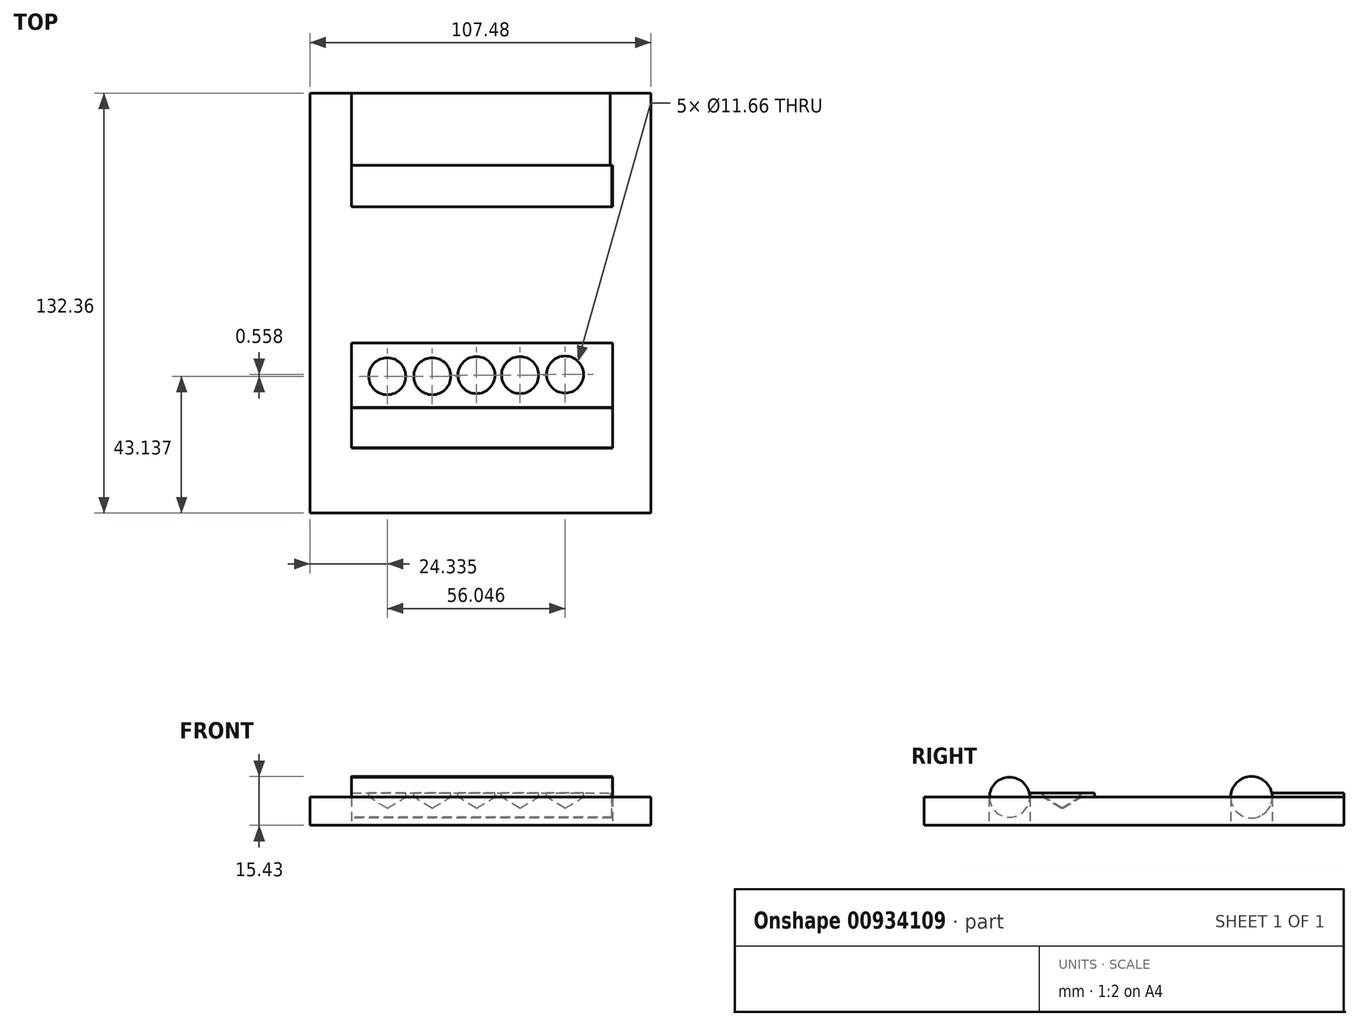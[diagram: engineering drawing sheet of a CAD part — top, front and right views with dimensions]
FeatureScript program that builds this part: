
annotation { "Feature Type Name" : "Feature", "Feature Type Description" : "" }
export const myFeature = defineFeature(function(context is Context, id is Id, definition is map)
    precondition{}
    {
        {
            var Q0;
            Q0=qCreatedBy(makeId("Top.planeOp"),FACE);
            var sketch = newSketch(context, id + "F0", { "sketchPlane" : qUnion([Q0])});
            skLineSegment(sketch, "E0.bottom", {"start": v(-52.45, 65.35) * mm, "end": v(55.03, 65.35) * mm});
            skLineSegment(sketch, "E0.top", {"start": v(-52.45, -67.01) * mm, "end": v(55.03, -67.01) * mm});
            skLineSegment(sketch, "E0.left", {"start": v(-52.45, 65.35) * mm, "end": v(-52.45, -67.01) * mm});
            skLineSegment(sketch, "E0.right", {"start": v(55.03, 65.35) * mm, "end": v(55.03, -67.01) * mm});
            skLineSegment(sketch, "E1.bottom", {"start": v(-39.36, 42.68) * mm, "end": v(42.86, 42.68) * mm});
            skLineSegment(sketch, "E1.top", {"start": v(-39.36, 29.59) * mm, "end": v(42.86, 29.59) * mm});
            skLineSegment(sketch, "E1.left", {"start": v(-39.36, 42.68) * mm, "end": v(-39.36, 29.59) * mm});
            skLineSegment(sketch, "E1.right", {"start": v(42.86, 42.68) * mm, "end": v(42.86, 29.59) * mm});
            skLineSegment(sketch, "E2.bottom", {"start": v(-39.36, -33.64) * mm, "end": v(42.86, -33.64) * mm});
            skLineSegment(sketch, "E2.top", {"start": v(-39.36, -46.55) * mm, "end": v(42.86, -46.55) * mm});
            skLineSegment(sketch, "E2.left", {"start": v(-39.36, -33.64) * mm, "end": v(-39.36, -46.55) * mm});
            skLineSegment(sketch, "E2.right", {"start": v(42.86, -33.64) * mm, "end": v(42.86, -46.55) * mm});
            skSolve(sketch);
        }
        {
            var Q0;
            Q0 = qSketchRegion(id + "F0", true);
            extrude(context, id + "F1", {"entities" : qUnion([Q0]), "depth" : 8.9 * mm, "offsetDistance" : 25.4 * mm});
        }
        {
            var Q0;
            Q0=makeQuery(id+"F1.opExtrude","SWEPT_FACE",FACE,{"disambiguationData":[OSD([sQuery(id+"F0.wireOp",EDGE,"E1.left")])]});
            var sketch = newSketch(context, id + "F2", { "sketchPlane" : qUnion([Q0])});
            skPoint(sketch, "E3", {"position": v(36.13, 8.9) * mm});
            skPoint(sketch, "E4", {"position": v(15.66, 189.85) * mm});
            skCircle(sketch, "E5", {"center": v(36.13, 8.9) * mm, "radius": 6.54 * mm});
            skSolve(sketch);
        }
        {
            var Q0;
            Q0 = qSketchRegion(id + "F2", true);
            extrude(context, id + "F3", {"entities" : qUnion([Q0]), "operationType" : NewBodyOperationType.ADD, "depth" : 82.04 * mm, "offsetDistance" : 25.4 * mm});
        }
        {
            var Q0;
            Q0=makeQuery(id+"F1.opExtrude","SWEPT_FACE",FACE,{"disambiguationData":[OSD([sQuery(id+"F0.wireOp",EDGE,"E2.left")])]});
            var sketch = newSketch(context, id + "F4", { "sketchPlane" : qUnion([Q0])});
            skPoint(sketch, "E6", {"position": v(-40.1, 8.9) * mm});
            skCircle(sketch, "E7", {"center": v(-40.1, 8.9) * mm, "radius": 6.32 * mm});
            skSolve(sketch);
        }
        {
            var Q0;
            Q0 = qSketchRegion(id + "F4", true);
            extrude(context, id + "F5", {"entities" : qUnion([Q0]), "operationType" : NewBodyOperationType.ADD, "depth" : 82.3 * mm, "offsetDistance" : 25.4 * mm});
        }
        {
            var Q0;
            Q0=makeQuery(id+"F1.opExtrude","CAP_FACE",FACE,{"disambiguationData":[OSD([sQuery(id+"F0.wireOp",EDGE,"E0.bottom"),sQuery(id+"F0.wireOp",EDGE,"E0.top"),sQuery(id+"F0.wireOp",EDGE,"E0.left"),sQuery(id+"F0.wireOp",EDGE,"E0.right"),sQuery(id+"F0.wireOp",EDGE,"E1.bottom"),sQuery(id+"F0.wireOp",EDGE,"E1.top"),sQuery(id+"F0.wireOp",EDGE,"E1.left"),sQuery(id+"F0.wireOp",EDGE,"E1.right"),sQuery(id+"F0.wireOp",EDGE,"E2.bottom"),sQuery(id+"F0.wireOp",EDGE,"E2.top"),sQuery(id+"F0.wireOp",EDGE,"E2.left"),sQuery(id+"F0.wireOp",EDGE,"E2.right")])],"isStart":false});
            var sketch = newSketch(context, id + "F6", { "sketchPlane" : qUnion([Q0])});
            skLineSegment(sketch, "E8.bottom", {"start": v(-39.36, 42.68) * mm, "end": v(42.17, 42.68) * mm});
            skLineSegment(sketch, "E8.top", {"start": v(-39.36, 65.35) * mm, "end": v(42.17, 65.35) * mm});
            skLineSegment(sketch, "E8.left", {"start": v(-39.36, 42.68) * mm, "end": v(-39.36, 65.35) * mm});
            skLineSegment(sketch, "E8.right", {"start": v(42.17, 42.68) * mm, "end": v(42.17, 65.35) * mm});
            skLineSegment(sketch, "E9.bottom", {"start": v(42.86, -33.64) * mm, "end": v(-39.36, -33.64) * mm});
            skLineSegment(sketch, "E9.top", {"start": v(42.86, -13.32) * mm, "end": v(-39.36, -13.32) * mm});
            skLineSegment(sketch, "E9.left", {"start": v(42.86, -33.64) * mm, "end": v(42.86, -13.32) * mm});
            skLineSegment(sketch, "E9.right", {"start": v(-39.36, -33.64) * mm, "end": v(-39.36, -13.32) * mm});
            skSolve(sketch);
        }
        {
            var Q0;
            Q0 = qSketchRegion(id + "F6", true);
            extrude(context, id + "F7", {"entities" : qUnion([Q0]), "operationType" : NewBodyOperationType.ADD, "depth" : 1.27 * mm, "offsetDistance" : 25.4 * mm});
        }
        {
            var Q0;
            Q0=makeQuery(id+"F7.opExtrude","CAP_FACE",FACE,{"disambiguationData":[OSD([sQuery(id+"F6.wireOp",EDGE,"E9.bottom"),sQuery(id+"F6.wireOp",EDGE,"E9.top"),sQuery(id+"F6.wireOp",EDGE,"E9.left"),sQuery(id+"F6.wireOp",EDGE,"E9.right")])],"isStart":false});
            var sketch = newSketch(context, id + "F8", { "sketchPlane" : qUnion([Q0])});
            skLineSegment(sketch, "E10.bottom", {"start": v(-34.75, -17.8) * mm, "end": v(37.15, -17.8) * mm});
            skLineSegment(sketch, "E10.top", {"start": v(-34.75, -33.64) * mm, "end": v(37.15, -33.64) * mm});
            skLineSegment(sketch, "E10.left", {"start": v(-34.75, -17.8) * mm, "end": v(-34.75, -33.64) * mm});
            skLineSegment(sketch, "E10.right", {"start": v(37.15, -17.8) * mm, "end": v(37.15, -33.64) * mm});
            skCircle(sketch, "E11", {"center": v(-28.11, -23.87) * mm, "radius": 6.09 * mm});
            skCircle(sketch, "E12", {"center": v(-13.92, -23.87) * mm, "radius": 5.9 * mm});
            skCircle(sketch, "E13", {"center": v(0, -23.5) * mm, "radius": 5.57 * mm});
            skCircle(sketch, "E14", {"center": v(13.74, -23.5) * mm, "radius": 5.62 * mm});
            skCircle(sketch, "E15", {"center": v(27.93, -23.32) * mm, "radius": 5.62 * mm});
            skSolve(sketch);
        }
        {
            var Q0;
            Q0=sQuery(id+"F8.wireOp",VERTEX,"E12.center");
            var Q1;
            Q1=sQuery(id+"F8.wireOp",VERTEX,"E13.center");
            var Q2;
            Q2=sQuery(id+"F8.wireOp",VERTEX,"E14.center");
            var Q3;
            Q3=sQuery(id+"F8.wireOp",VERTEX,"E15.center");
            var Q4;
            Q4=sQuery(id+"F8.wireOp",VERTEX,"E11.center");
            var Q5;
            Q5=makeQuery(id+"F1.opExtrude","SWEPT_BODY",BODY,{"disambiguationData":[OSD([sQuery(id+"F0.wireOp",EDGE,"E0.bottom"),sQuery(id+"F0.wireOp",EDGE,"E0.top"),sQuery(id+"F0.wireOp",EDGE,"E0.left"),sQuery(id+"F0.wireOp",EDGE,"E0.right"),sQuery(id+"F0.wireOp",EDGE,"E1.bottom"),sQuery(id+"F0.wireOp",EDGE,"E1.top"),sQuery(id+"F0.wireOp",EDGE,"E1.left"),sQuery(id+"F0.wireOp",EDGE,"E1.right"),sQuery(id+"F0.wireOp",EDGE,"E2.bottom"),sQuery(id+"F0.wireOp",EDGE,"E2.top"),sQuery(id+"F0.wireOp",EDGE,"E2.left"),sQuery(id+"F0.wireOp",EDGE,"E2.right")])]});
            hole(context, id + "F9", {"style" : HoleStyle.SIMPLE, "endStyle" : HoleEndStyle.BLIND, "holeDiameter" : 11.66 * mm, "majorDiameter" : 6.35 * mm, "holeDepth" : 1.27 * mm, "isTappedThrough" : true, "tappedDepth" : 12.7 * mm, "tapClearance" : 3, "locations" : qUnion([Q0, Q1, Q2, Q3, Q4]), "scope" : qUnion([Q5])});
        }
    });
